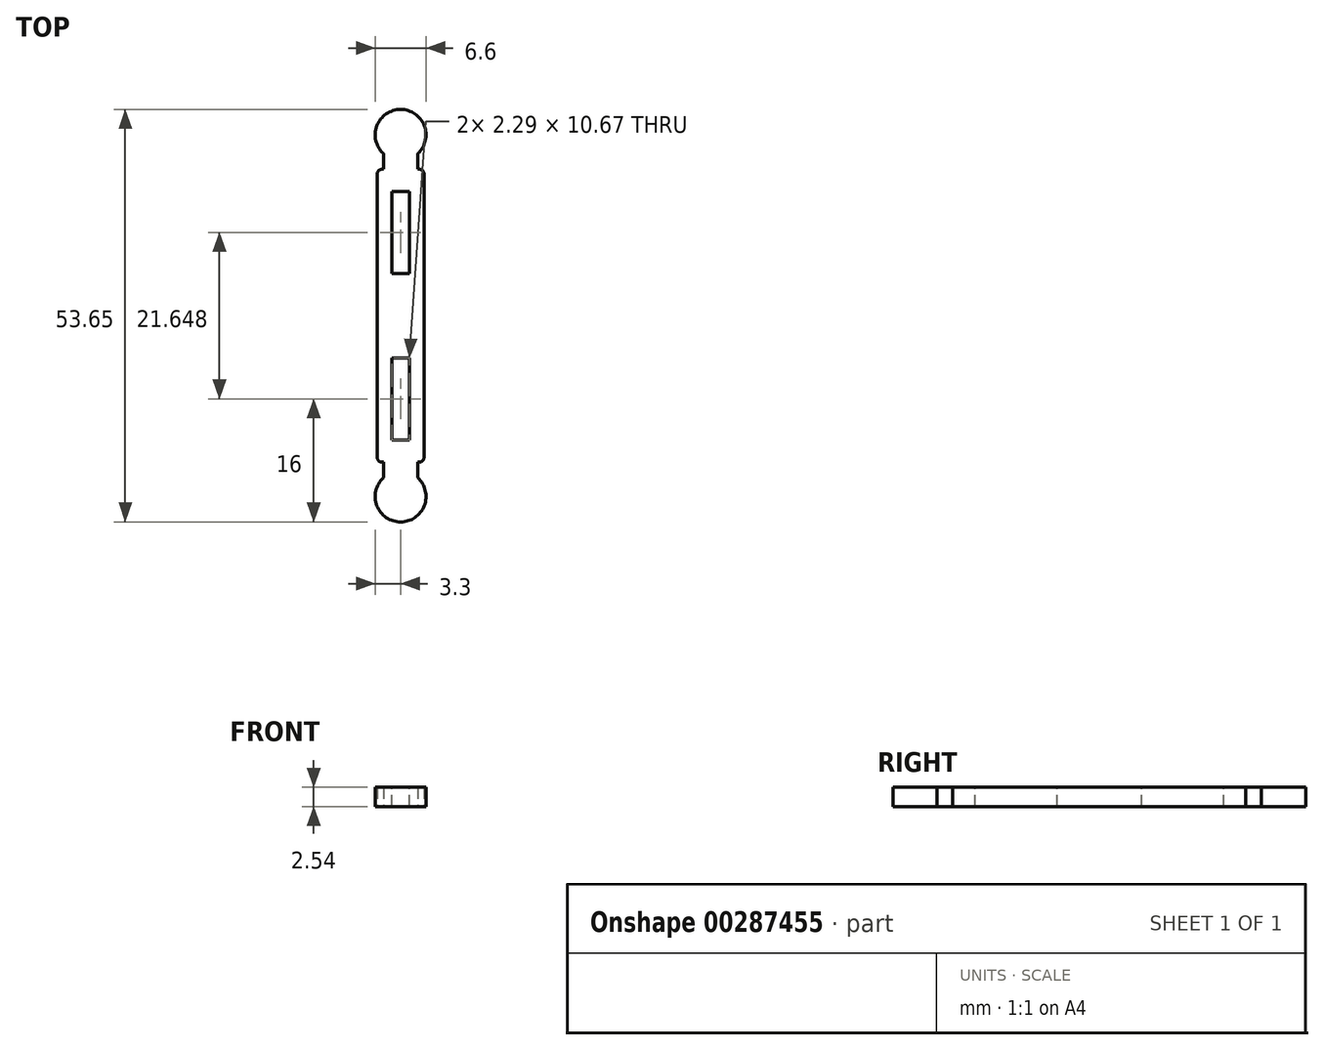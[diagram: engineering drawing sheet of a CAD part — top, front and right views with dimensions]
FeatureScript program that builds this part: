
annotation { "Feature Type Name" : "Feature", "Feature Type Description" : "" }
export const myFeature = defineFeature(function(context is Context, id is Id, definition is map)
    precondition{}
    {
        {
            var Q0;
            Q0=qCreatedBy(makeId("Top.planeOp"),FACE);
            var sketch = newSketch(context, id + "F0", { "sketchPlane" : qUnion([Q0])});
            skCircle(sketch, "E0", {"center": v(0, 0) * mm, "radius": 3.3 * mm});
            skSolve(sketch);
        }
        {
            var Q0;
            Q0=qSketchRegion(id+"F0",true);
            extrude(context, id + "F1", {"entities" : qUnion([Q0]), "depth" : 2.54 * mm});
        }
        {
            var Q0;
            Q0=makeQuery(id+"F1.opExtrude","CAP_FACE",FACE,{"disambiguationData":[OSD([sQuery(id+"F0.wireOp",EDGE,"E0")])],"isStart":true});
            var sketch = newSketch(context, id + "F2", { "sketchPlane" : qUnion([Q0])});
            skLineSegment(sketch, "E1.bottom", {"start": v(-2.22, -2.44) * mm, "end": v(2.22, -2.44) * mm});
            skLineSegment(sketch, "E1.top", {"start": v(-2.22, -4.47) * mm, "end": v(2.22, -4.47) * mm});
            skLineSegment(sketch, "E1.left", {"start": v(-2.22, -2.44) * mm, "end": v(-2.22, -4.47) * mm});
            skLineSegment(sketch, "E1.right", {"start": v(2.22, -2.44) * mm, "end": v(2.22, -4.47) * mm});
            skSolve(sketch);
        }
        {
            var Q0;
            Q0=makeQuery(id+"F2.imprint","IMPRINT",FACE,{"disambiguationData":[TD([[makeQuery(id+"F2.imprint","IMPRINT",EDGE,{"derivedFrom":sQuery(id+"F2.wireOp",EDGE,"E1.top")}),1.0]])]});
            var Q1;
            Q1=makeQuery(id+"F1.opExtrude","CAP_FACE",FACE,{"disambiguationData":[OSD([sQuery(id+"F0.wireOp",EDGE,"E0")])],"isStart":false});
            extrude(context, id + "F3", {"entities" : qUnion([Q0]), "operationType" : NewBodyOperationType.ADD, "endBound" : BoundingType.UP_TO_SURFACE, "oppositeDirection" : true, "endBoundEntityFace" : qUnion([Q1]), "depth" : 25.4 * mm});
        }
        {
            var Q0;
            Q0=qCreatedBy(makeId("Top.planeOp"),FACE);
            var sketch = newSketch(context, id + "F4", { "sketchPlane" : qUnion([Q0])});
            skLineSegment(sketch, "E2.bottom", {"start": v(-3.05, 4.47) * mm, "end": v(3.05, 4.47) * mm});
            skLineSegment(sketch, "E2.top", {"start": v(-3.05, 23.52) * mm, "end": v(3.05, 23.52) * mm});
            skLineSegment(sketch, "E2.left", {"start": v(-3.05, 4.47) * mm, "end": v(-3.05, 23.52) * mm});
            skLineSegment(sketch, "E2.right", {"start": v(3.05, 4.47) * mm, "end": v(3.05, 23.52) * mm});
            skSolve(sketch);
        }
        {
            var Q0;
            Q0=qSketchRegion(id+"F4",true);
            var Q1;
            {var subQ0=sQuery(id+"F0.wireOp",EDGE,"E0");Q1=makeQuery(id+"F3.boolean.opBoolean","MERGE",FACE,{"derivedFrom":[makeQuery(id+"F1.opExtrude","CAP_FACE",FACE,{"disambiguationData":[OSD([subQ0])],"isStart":false}),makeQuery(id+"F3.opExtrude","CAP_FACE",FACE,{"disambiguationData":[OSD([subQ0])],"isStart":false})]});}
            extrude(context, id + "F5", {"entities" : qUnion([Q0]), "operationType" : NewBodyOperationType.ADD, "endBound" : BoundingType.UP_TO_SURFACE, "endBoundEntityFace" : qUnion([Q1]), "depth" : 25.4 * mm});
        }
        {
            var Q0;
            Q0=makeQuery(id+"F5.opExtrude","SWEPT_EDGE",EDGE,{"disambiguationData":[OSD([sQuery(id+"F4.wireOp",EDGE,"E2.bottom"),sQuery(id+"F4.wireOp",EDGE,"E2.right")])]});
            var Q1;
            Q1=makeQuery(id+"F5.opExtrude","SWEPT_EDGE",EDGE,{"disambiguationData":[OSD([sQuery(id+"F4.wireOp",EDGE,"E2.bottom"),sQuery(id+"F4.wireOp",EDGE,"E2.left")])]});
            fillet(context, id + "F6", {"entities" : qUnion([Q0, Q1]), "radius" : 0.64 * mm, "tangentPropagation" : true, "allowEdgeOverflow" : false});
        }
        {
            var Q0;
            {var subQ0=sQuery(id+"F0.wireOp",EDGE,"E0");Q0=makeQuery(id+"F5.boolean.opBoolean","MERGE",FACE,{"derivedFrom":[makeQuery(id+"F3.boolean.opBoolean","MERGE",FACE,{"derivedFrom":[makeQuery(id+"F1.opExtrude","CAP_FACE",FACE,{"disambiguationData":[OSD([subQ0])],"isStart":false}),makeQuery(id+"F3.opExtrude","CAP_FACE",FACE,{"disambiguationData":[OSD([subQ0])],"isStart":false})]}),makeQuery(id+"F5.opExtrude","CAP_FACE",FACE,{"disambiguationData":[OSD([subQ0])],"isStart":false})]});}
            var sketch = newSketch(context, id + "F7", { "sketchPlane" : qUnion([Q0])});
            skLineSegment(sketch, "E3.bottom", {"start": v(1.14, 7.37) * mm, "end": v(-1.14, 7.37) * mm});
            skLineSegment(sketch, "E3.top", {"start": v(1.14, 18.03) * mm, "end": v(-1.14, 18.03) * mm});
            skLineSegment(sketch, "E3.left", {"start": v(1.14, 7.37) * mm, "end": v(1.14, 18.03) * mm});
            skLineSegment(sketch, "E3.right", {"start": v(-1.14, 7.37) * mm, "end": v(-1.14, 18.03) * mm});
            skPoint(sketch, "E3.middle", {"position": v(0, 12.7) * mm});
            skSolve(sketch);
        }
        {
            var Q0;
            Q0=makeQuery(id+"F7.imprint","IMPRINT",FACE,{"disambiguationData":[TD([[makeQuery(id+"F7.imprint","IMPRINT",EDGE,{"derivedFrom":sQuery(id+"F7.wireOp",EDGE,"E3.bottom")}),-1.0]])]});
            extrude(context, id + "F8", {"entities" : qUnion([Q0]), "operationType" : NewBodyOperationType.REMOVE, "oppositeDirection" : true, "depth" : 25.4 * mm});
        }
        {
            var Q0;
            Q0=makeQuery(id+"F1.opExtrude","SWEPT_BODY",BODY,{"disambiguationData":[OSD([sQuery(id+"F0.wireOp",EDGE,"E0")])]});
            var Q1;
            Q1=makeQuery(id+"F5.opExtrude","SWEPT_FACE",FACE,{"disambiguationData":[OSD([sQuery(id+"F4.wireOp",EDGE,"E2.top")])]});
            mirror(context, id + "F9", {"operationType" : NewBodyOperationType.ADD, "entities" : qUnion([Q0]), "mirrorPlane" : qUnion([Q1])});
        }
    });
